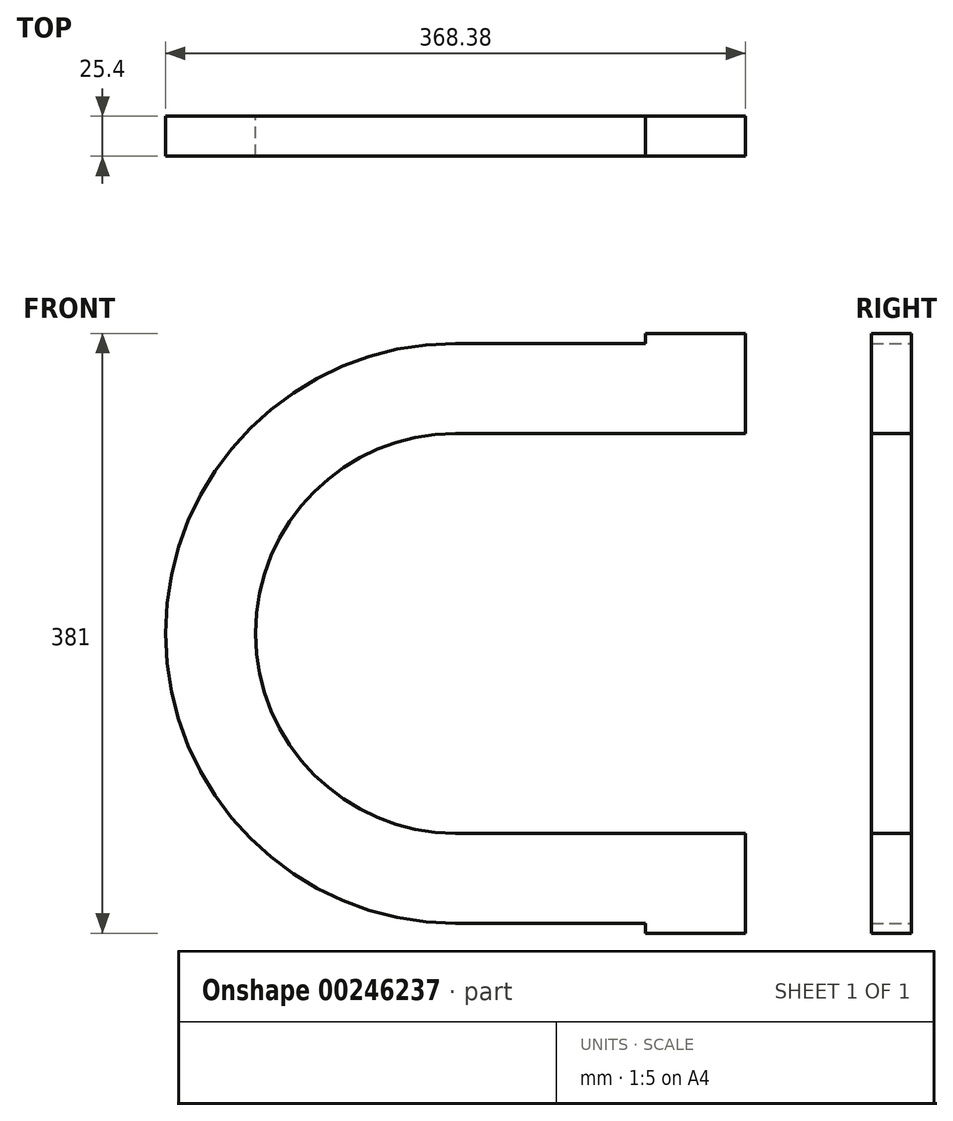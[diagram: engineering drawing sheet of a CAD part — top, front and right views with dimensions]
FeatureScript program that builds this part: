
annotation { "Feature Type Name" : "Feature", "Feature Type Description" : "" }
export const myFeature = defineFeature(function(context is Context, id is Id, definition is map)
    precondition{}
    {
        {
            var Q0;
            Q0=qCreatedBy(makeId("Front.planeOp"),FACE);
            var sketch = newSketch(context, id + "F0", { "sketchPlane" : qUnion([Q0])});
            skLineSegment(sketch, "E0.bottom", {"start": v(0, 184.19) * mm, "end": v(120.69, 184.19) * mm});
            skLineSegment(sketch, "E0.top", {"start": v(0, -184.19) * mm, "end": v(120.69, -184.19) * mm});
            skLineSegment(sketch, "E0.right", {"start": v(184.19, 184.19) * mm, "end": v(184.19, 127) * mm});
            skPoint(sketch, "E0.middle", {"position": v(0, 0) * mm});
            skArc(sketch, "E1", {"start": v(0, 127) * mm, "mid": v(-127, 0) * mm, "end": v(0, -127) * mm});
            skLineSegment(sketch, "E2", {"start": v(0, -127) * mm, "end": v(184.19, -127) * mm});
            skLineSegment(sketch, "E3", {"start": v(0, 127) * mm, "end": v(184.19, 127) * mm});
            skLineSegment(sketch, "E4.bottom", {"start": v(184.19, -127) * mm, "end": v(120.69, -127) * mm});
            skLineSegment(sketch, "E4.top", {"start": v(184.19, -190.5) * mm, "end": v(120.69, -190.5) * mm});
            skLineSegment(sketch, "E4.left", {"start": v(184.19, -127) * mm, "end": v(184.19, -190.5) * mm});
            skLineSegment(sketch, "E4.right", {"start": v(120.69, -184.19) * mm, "end": v(120.69, -190.5) * mm});
            skLineSegment(sketch, "E5.bottom", {"start": v(184.19, 127) * mm, "end": v(120.69, 127) * mm});
            skLineSegment(sketch, "E5.top", {"start": v(184.19, 190.5) * mm, "end": v(120.69, 190.5) * mm});
            skLineSegment(sketch, "E5.left", {"start": v(184.19, 127) * mm, "end": v(184.19, 190.5) * mm});
            skLineSegment(sketch, "E5.right", {"start": v(120.69, 184.19) * mm, "end": v(120.69, 190.5) * mm});
            skArc(sketch, "E6", {"start": v(0, 184.19) * mm, "mid": v(-184.19, 0) * mm, "end": v(0, -184.19) * mm});
            skPoint(sketch, "E6.first.point", {"position": v(0, -184.19) * mm});
            skPoint(sketch, "E6.second.point", {"position": v(-184.19, 0) * mm});
            skPoint(sketch, "E6.third.point", {"position": v(0, 184.19) * mm});
            skPoint(sketch, "E7.orphan", {"position": v(-184.19, -184.19) * mm});
            skPoint(sketch, "E8.orphan", {"position": v(-184.19, 184.19) * mm});
            skLineSegment(sketch, "E9.trimOffspring", {"start": v(184.19, -127) * mm, "end": v(184.19, -184.19) * mm});
            skSolve(sketch);
        }
        {
            var Q0;
            Q0 = qSketchRegion(id + "F0", true);
            extrude(context, id + "F1", {"entities" : qUnion([Q0]), "depth" : 25.4 * mm});
        }
    });
